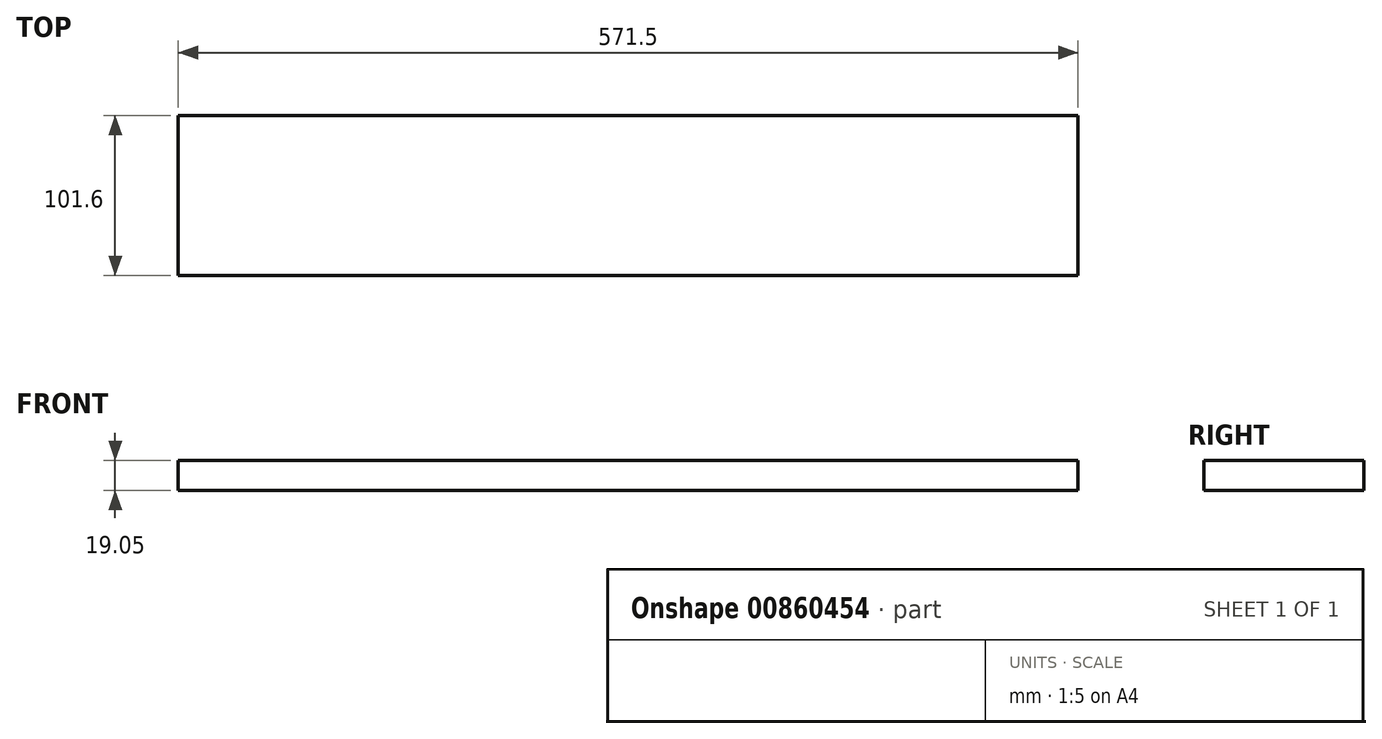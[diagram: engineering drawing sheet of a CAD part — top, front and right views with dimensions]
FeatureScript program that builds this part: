
annotation { "Feature Type Name" : "Feature", "Feature Type Description" : "" }
export const myFeature = defineFeature(function(context is Context, id is Id, definition is map)
    precondition{}
    {
        {
            var Q0;
            Q0=qCreatedBy(makeId("Top.planeOp"),FACE);
            var sketch = newSketch(context, id + "F0", { "sketchPlane" : qUnion([Q0])});
            skLineSegment(sketch, "E0.bottom", {"start": v(-285.75, 50.8) * mm, "end": v(285.75, 50.8) * mm});
            skLineSegment(sketch, "E0.top", {"start": v(-285.75, -50.8) * mm, "end": v(285.75, -50.8) * mm});
            skLineSegment(sketch, "E0.left", {"start": v(-285.75, 50.8) * mm, "end": v(-285.75, -50.8) * mm});
            skLineSegment(sketch, "E0.right", {"start": v(285.75, 50.8) * mm, "end": v(285.75, -50.8) * mm});
            skPoint(sketch, "E0.middle", {"position": v(0, 0) * mm});
            skSolve(sketch);
        }
        {
            var Q0;
            Q0=makeQuery(id+"F0.imprint","IMPRINT",FACE,{"disambiguationData":[TD([[makeQuery(id+"F0.imprint","IMPRINT",EDGE,{"derivedFrom":sQuery(id+"F0.wireOp",EDGE,"E0.bottom")}),-1.0]])]});
            extrude(context, id + "F1", {"entities" : qUnion([Q0]), "depth" : 19.05 * mm, "offsetDistance" : 25.4 * mm});
        }
    });
